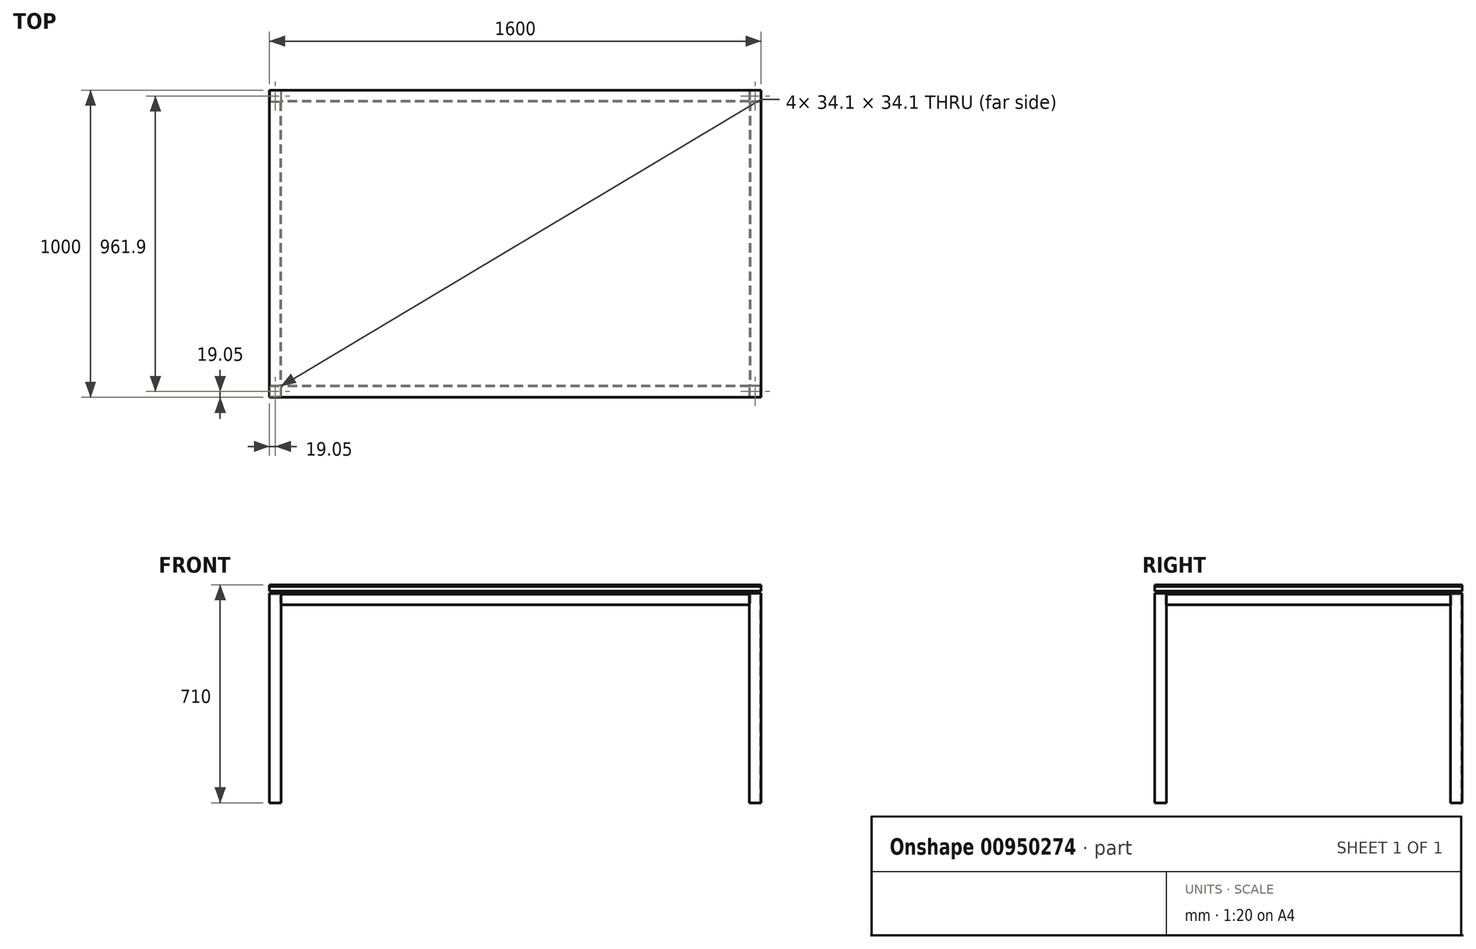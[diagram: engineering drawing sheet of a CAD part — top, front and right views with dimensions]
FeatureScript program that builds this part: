
annotation { "Feature Type Name" : "Feature", "Feature Type Description" : "" }
export const myFeature = defineFeature(function(context is Context, id is Id, definition is map)
    precondition{}
    {
        {
            var Q0;
            Q0=qCreatedBy(makeId("Top.planeOp"),FACE);
            var sketch = newSketch(context, id + "F0", { "sketchPlane" : qUnion([Q0])});
            skLineSegment(sketch, "E0.bottom", {"start": v(-800, -500) * mm, "end": v(800, -500) * mm});
            skLineSegment(sketch, "E0.top", {"start": v(-800, 500) * mm, "end": v(800, 500) * mm});
            skLineSegment(sketch, "E0.left", {"start": v(-800, -500) * mm, "end": v(-800, 500) * mm});
            skLineSegment(sketch, "E0.right", {"start": v(800, -500) * mm, "end": v(800, 500) * mm});
            skPoint(sketch, "E0.middle", {"position": v(0, 0) * mm});
            skSolve(sketch);
        }
        {
            var Q0;
            Q0 = qSketchRegion(id + "F0", true);
            extrude(context, id + "F1", {"entities" : qUnion([Q0]), "depth" : 15 * mm, "offsetDistance" : 25 * mm});
        }
        {
            var Q0;
            Q0=makeQuery(id+"F1.opExtrude","CAP_FACE",FACE,{"disambiguationData":[OSD([sQuery(id+"F0.wireOp",EDGE,"E0.bottom"),sQuery(id+"F0.wireOp",EDGE,"E0.top"),sQuery(id+"F0.wireOp",EDGE,"E0.left"),sQuery(id+"F0.wireOp",EDGE,"E0.right")])],"isStart":true});
            cPlane(context, id + "F2", {"entities" : qUnion([Q0]), "cplaneType" : CPlaneType.OFFSET, "offset" : 6 * mm, "width" : 150 * mm, "height" : 150 * mm});
        }
        {
            var Q0;
            Q0=qCreatedBy(id+"F2.planeOp",FACE);
            var sketch = newSketch(context, id + "F3", { "sketchPlane" : qUnion([Q0])});
            skLineSegment(sketch, "E1.bottom", {"start": v(-800, 500) * mm, "end": v(-761.9, 500) * mm});
            skLineSegment(sketch, "E1.top", {"start": v(-800, 461.9) * mm, "end": v(-761.9, 461.9) * mm});
            skLineSegment(sketch, "E1.left", {"start": v(-800, 500) * mm, "end": v(-800, 461.9) * mm});
            skLineSegment(sketch, "E1.right", {"start": v(-761.9, 500) * mm, "end": v(-761.9, 461.9) * mm});
            skLineSegment(sketch, "E2", {"start": v(0, 0) * mm, "end": v(0, 498.56) * mm, "construction": true});
            skLineSegment(sketch, "E3", {"start": v(0, 0) * mm, "end": v(814.8, 0) * mm, "construction": true});
            skLineSegment(sketch, "E4.bottom", {"start": v(-798, 498) * mm, "end": v(-763.9, 498) * mm});
            skLineSegment(sketch, "E4.top", {"start": v(-798, 463.9) * mm, "end": v(-763.9, 463.9) * mm});
            skLineSegment(sketch, "E4.left", {"start": v(-798, 498) * mm, "end": v(-798, 463.9) * mm});
            skLineSegment(sketch, "E4.right", {"start": v(-763.9, 498) * mm, "end": v(-763.9, 463.9) * mm});
            skPoint(sketch, "E4.middle", {"position": v(-780.95, 480.95) * mm});
            skPoint(sketch, "E4.middle.positionSnap0", {"position": v(-800, 480.95) * mm});
            skPoint(sketch, "E4.middle.positionSnap1", {"position": v(-780.95, 500) * mm});
            skPoint(sketch, "E4.centerSnap0", {"position": v(-800, 480.95) * mm});
            skPoint(sketch, "E4.centerSnap1", {"position": v(-780.95, 500) * mm});
            skPoint(sketch, "E5.MirrorP", {"position": v(780.95, 500) * mm});
            skPoint(sketch, "E6.MirrorP", {"position": v(800, 480.95) * mm});
            skLineSegment(sketch, "E7.MirrorCS", {"start": v(800, 461.9) * mm, "end": v(761.9, 461.9) * mm});
            skPoint(sketch, "E8.MirrorP", {"position": v(780.95, 480.95) * mm});
            skLineSegment(sketch, "E9.MirrorCS", {"start": v(800, 500) * mm, "end": v(761.9, 500) * mm});
            skLineSegment(sketch, "E10.MirrorCS", {"start": v(763.9, 498) * mm, "end": v(763.9, 463.9) * mm});
            skLineSegment(sketch, "E11.MirrorCS", {"start": v(798, 498) * mm, "end": v(763.9, 498) * mm});
            skLineSegment(sketch, "E12.MirrorCS", {"start": v(761.9, 500) * mm, "end": v(761.9, 461.9) * mm});
            skLineSegment(sketch, "E13.MirrorCS", {"start": v(798, 498) * mm, "end": v(798, 463.9) * mm});
            skLineSegment(sketch, "E14.MirrorCS", {"start": v(800, 500) * mm, "end": v(800, 461.9) * mm});
            skLineSegment(sketch, "E15.MirrorCS", {"start": v(798, 463.9) * mm, "end": v(763.9, 463.9) * mm});
            skLineSegment(sketch, "E16.MirrorCS", {"start": v(-800, -500) * mm, "end": v(-761.9, -500) * mm});
            skLineSegment(sketch, "E17.MirrorCS", {"start": v(-800, -500) * mm, "end": v(-800, -461.9) * mm});
            skLineSegment(sketch, "E18.MirrorCS", {"start": v(798, -463.9) * mm, "end": v(763.9, -463.9) * mm});
            skLineSegment(sketch, "E19.MirrorCS", {"start": v(763.9, -498) * mm, "end": v(763.9, -463.9) * mm});
            skLineSegment(sketch, "E20.MirrorCS", {"start": v(-798, -463.9) * mm, "end": v(-763.9, -463.9) * mm});
            skLineSegment(sketch, "E21.MirrorCS", {"start": v(800, -500) * mm, "end": v(761.9, -500) * mm});
            skLineSegment(sketch, "E22.MirrorCS", {"start": v(-798, -498) * mm, "end": v(-763.9, -498) * mm});
            skLineSegment(sketch, "E23.MirrorCS", {"start": v(-798, -498) * mm, "end": v(-798, -463.9) * mm});
            skLineSegment(sketch, "E24.MirrorCS", {"start": v(761.9, -500) * mm, "end": v(761.9, -461.9) * mm});
            skLineSegment(sketch, "E25.MirrorCS", {"start": v(798, -498) * mm, "end": v(798, -463.9) * mm});
            skLineSegment(sketch, "E26.MirrorCS", {"start": v(800, -500) * mm, "end": v(800, -461.9) * mm});
            skLineSegment(sketch, "E27.MirrorCS", {"start": v(798, -498) * mm, "end": v(763.9, -498) * mm});
            skLineSegment(sketch, "E28.MirrorCS", {"start": v(-800, -461.9) * mm, "end": v(-761.9, -461.9) * mm});
            skLineSegment(sketch, "E29.MirrorCS", {"start": v(-761.9, -500) * mm, "end": v(-761.9, -461.9) * mm});
            skLineSegment(sketch, "E30.MirrorCS", {"start": v(800, -461.9) * mm, "end": v(761.9, -461.9) * mm});
            skLineSegment(sketch, "E31.MirrorCS", {"start": v(-763.9, -498) * mm, "end": v(-763.9, -463.9) * mm});
            skPoint(sketch, "E32.MirrorP", {"position": v(-800, -480.95) * mm});
            skPoint(sketch, "E33.MirrorP", {"position": v(800, -480.95) * mm});
            skPoint(sketch, "E34.MirrorP", {"position": v(780.95, -500) * mm});
            skPoint(sketch, "E35.MirrorP", {"position": v(-780.95, -500) * mm});
            skPoint(sketch, "E36.MirrorP", {"position": v(-780.95, -480.95) * mm});
            skPoint(sketch, "E37.MirrorP", {"position": v(780.95, -480.95) * mm});
            skSolve(sketch);
        }
        {
            var Q0;
            Q0 = qSketchRegion(id + "F3", true);
            extrude(context, id + "F4", {"entities" : qUnion([Q0]), "depth" : 683 * mm, "offsetDistance" : 25 * mm});
        }
        {
            var Q0;
            Q0=makeQuery(id+"F4.opExtrude","SWEPT_FACE",FACE,{"disambiguationData":[OSD([sQuery(id+"F3.wireOp",EDGE,"E1.right")])]});
            var sketch = newSketch(context, id + "F5", { "sketchPlane" : qUnion([Q0])});
            skLineSegment(sketch, "E38", {"start": v(-500, -6) * mm, "end": v(-461.9, -6) * mm});
            skLineSegment(sketch, "E39", {"start": v(-461.9, -6) * mm, "end": v(-461.9, -44.1) * mm});
            skLineSegment(sketch, "E40", {"start": v(-461.9, -44.1) * mm, "end": v(-465.4, -44.1) * mm});
            skLineSegment(sketch, "E41", {"start": v(-465.4, -44.1) * mm, "end": v(-465.4, -9.5) * mm});
            skLineSegment(sketch, "E42", {"start": v(-465.4, -9.5) * mm, "end": v(-500, -9.5) * mm});
            skLineSegment(sketch, "E43", {"start": v(-500, -9.5) * mm, "end": v(-500, -6) * mm});
            skSolve(sketch);
        }
        {
            var Q0;
            Q0 = qSketchRegion(id + "F5", true);
            var Q1;
            Q1=makeQuery(id+"F4.opExtrude","SWEPT_FACE",FACE,{"disambiguationData":[OSD([sQuery(id+"F3.wireOp",EDGE,"E12.MirrorCS")])]});
            extrude(context, id + "F6", {"entities" : qUnion([Q0]), "endBound" : BoundingType.UP_TO_SURFACE, "depth" : 25 * mm, "endBoundEntityFace" : qUnion([Q1]), "offsetDistance" : 25 * mm});
        }
        {
            var Q0;
            Q0=makeQuery(id+"F6.opExtrude","SWEPT_BODY",BODY,{"disambiguationData":[OSD([sQuery(id+"F5.wireOp",EDGE,"E38"),sQuery(id+"F5.wireOp",EDGE,"E39"),sQuery(id+"F5.wireOp",EDGE,"E40"),sQuery(id+"F5.wireOp",EDGE,"E41"),sQuery(id+"F5.wireOp",EDGE,"E42"),sQuery(id+"F5.wireOp",EDGE,"E43")])]});
            var Q1;
            Q1=qCreatedBy(makeId("Front.planeOp"),FACE);
            mirror(context, id + "F7", {"entities" : qUnion([Q0]), "mirrorPlane" : qUnion([Q1])});
        }
        {
            var Q0;
            Q0=makeQuery(id+"F4.opExtrude","SWEPT_FACE",FACE,{"disambiguationData":[OSD([sQuery(id+"F3.wireOp",EDGE,"E1.top")])]});
            var sketch = newSketch(context, id + "F8", { "sketchPlane" : qUnion([Q0])});
            skLineSegment(sketch, "E44", {"start": v(800, -6) * mm, "end": v(761.9, -6) * mm});
            skLineSegment(sketch, "E45", {"start": v(761.9, -6) * mm, "end": v(761.9, -44.1) * mm});
            skLineSegment(sketch, "E46", {"start": v(761.9, -44.1) * mm, "end": v(765.4, -44.1) * mm});
            skLineSegment(sketch, "E47", {"start": v(765.4, -44.1) * mm, "end": v(765.4, -9.5) * mm});
            skLineSegment(sketch, "E48", {"start": v(765.4, -9.5) * mm, "end": v(800, -9.5) * mm});
            skLineSegment(sketch, "E49", {"start": v(800, -9.5) * mm, "end": v(800, -6) * mm});
            skSolve(sketch);
        }
        {
            var Q0;
            Q0 = qSketchRegion(id + "F8", true);
            var Q1;
            Q1=makeQuery(id+"F4.opExtrude","SWEPT_FACE",FACE,{"disambiguationData":[OSD([sQuery(id+"F3.wireOp",EDGE,"E28.MirrorCS")])]});
            extrude(context, id + "F9", {"entities" : qUnion([Q0]), "endBound" : BoundingType.UP_TO_SURFACE, "depth" : 587 * mm, "endBoundEntityFace" : qUnion([Q1]), "offsetDistance" : 25 * mm});
        }
        {
            var Q0;
            Q0=makeQuery(id+"F9.opExtrude","SWEPT_BODY",BODY,{"disambiguationData":[OSD([sQuery(id+"F8.wireOp",EDGE,"E44"),sQuery(id+"F8.wireOp",EDGE,"E45"),sQuery(id+"F8.wireOp",EDGE,"E46"),sQuery(id+"F8.wireOp",EDGE,"E47"),sQuery(id+"F8.wireOp",EDGE,"E48"),sQuery(id+"F8.wireOp",EDGE,"E49")])]});
            var Q1;
            Q1=qCreatedBy(makeId("Right.planeOp"),FACE);
            mirror(context, id + "F10", {"entities" : qUnion([Q0]), "mirrorPlane" : qUnion([Q1])});
        }
        {
            var Q0;
            Q0=makeQuery(id+"F1.opExtrude","CAP_FACE",FACE,{"disambiguationData":[OSD([sQuery(id+"F0.wireOp",EDGE,"E0.bottom"),sQuery(id+"F0.wireOp",EDGE,"E0.top"),sQuery(id+"F0.wireOp",EDGE,"E0.left"),sQuery(id+"F0.wireOp",EDGE,"E0.right")])],"isStart":false});
            extrude(context, id + "F11", {"entities" : qUnion([Q0]), "depth" : 6 * mm, "offsetDistance" : 25 * mm});
        }
    });
